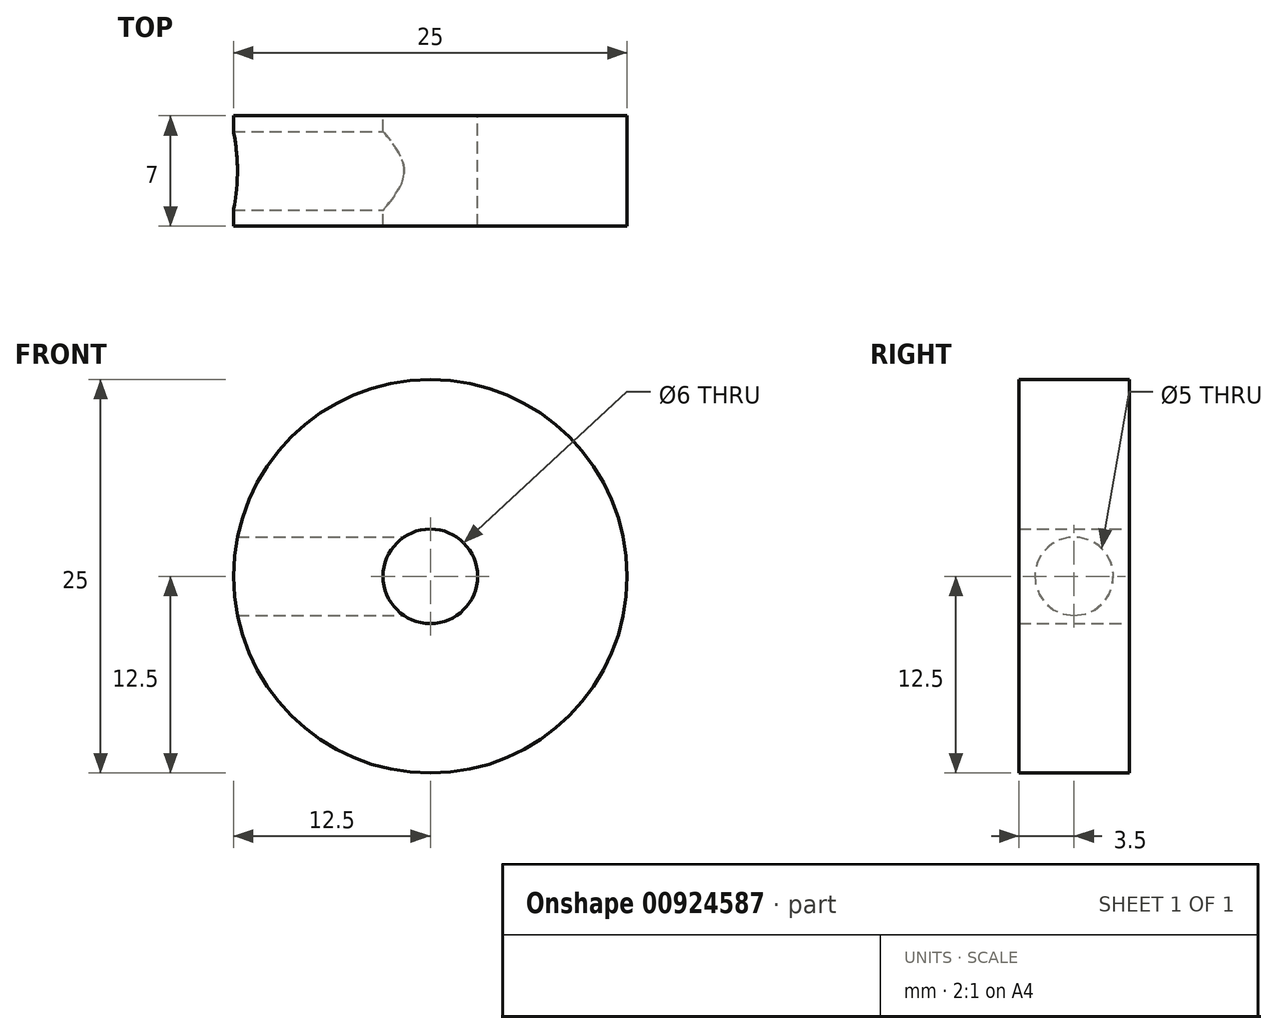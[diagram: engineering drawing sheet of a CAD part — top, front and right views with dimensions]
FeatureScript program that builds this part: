
annotation { "Feature Type Name" : "Feature", "Feature Type Description" : "" }
export const myFeature = defineFeature(function(context is Context, id is Id, definition is map)
    precondition{}
    {
        {
            var Q0;
            Q0=qCreatedBy(makeId("Front.planeOp"),FACE);
            var sketch = newSketch(context, id + "F0", { "sketchPlane" : qUnion([Q0])});
            skCircle(sketch, "E0", {"center": v(0, 0) * mm, "radius": 12.5 * mm});
            skCircle(sketch, "E1", {"center": v(0, 0) * mm, "radius": 3 * mm});
            skSolve(sketch);
        }
        {
            var Q0;
            Q0=makeQuery(id+"F0.imprint","IMPRINT",FACE,{"disambiguationData":[TD([[makeQuery(id+"F0.imprint","IMPRINT",EDGE,{"derivedFrom":sQuery(id+"F0.wireOp",EDGE,"E0")}),1.0]])]});
            extrude(context, id + "F1", {"entities" : qUnion([Q0]), "depth" : 7 * mm, "offsetDistance" : 25 * mm});
        }
        {
            var Q0;
            Q0=qCreatedBy(makeId("Right.planeOp"),FACE);
            var sketch = newSketch(context, id + "F2", { "sketchPlane" : qUnion([Q0])});
            skCircle(sketch, "E2", {"center": v(-3.5, 0) * mm, "radius": 2.5 * mm});
            skSolve(sketch);
        }
        {
            var Q0;
            Q0=makeQuery(id+"F2.imprint","IMPRINT",FACE,{"disambiguationData":[TD([[makeQuery(id+"F2.imprint","IMPRINT",EDGE,{"derivedFrom":sQuery(id+"F2.wireOp",EDGE,"E2")}),1.0]])]});
            extrude(context, id + "F3", {"entities" : qUnion([Q0]), "operationType" : NewBodyOperationType.REMOVE, "oppositeDirection" : true, "depth" : 25 * mm, "offsetDistance" : 25 * mm});
        }
    });
